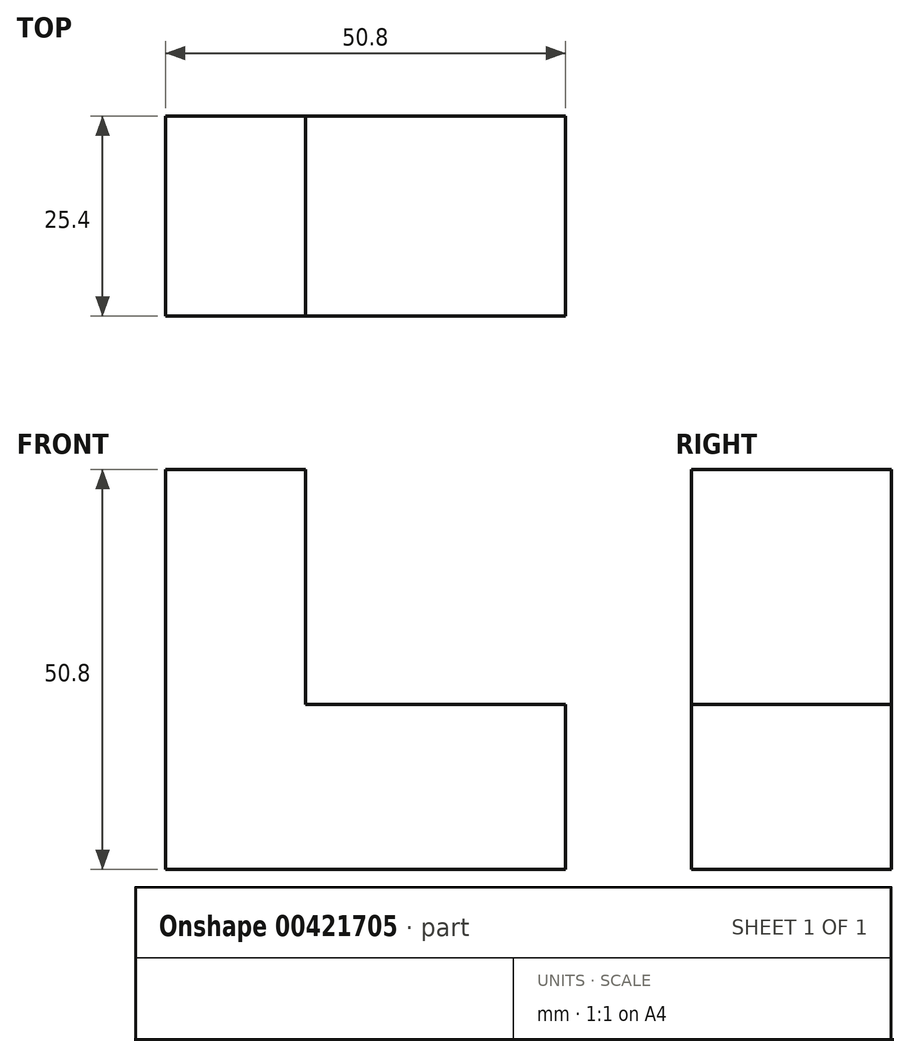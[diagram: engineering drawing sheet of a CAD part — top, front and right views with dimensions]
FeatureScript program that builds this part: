
annotation { "Feature Type Name" : "Feature", "Feature Type Description" : "" }
export const myFeature = defineFeature(function(context is Context, id is Id, definition is map)
    precondition{}
    {
        {
            var Q0;
            Q0=qCreatedBy(makeId("Front.planeOp"),FACE);
            var sketch = newSketch(context, id + "F0", { "sketchPlane" : qUnion([Q0])});
            skLineSegment(sketch, "E0", {"start": v(0, 0) * mm, "end": v(50.8, 0) * mm});
            skLineSegment(sketch, "E1", {"start": v(50.8, 0) * mm, "end": v(50.8, 50.8) * mm});
            skLineSegment(sketch, "E2", {"start": v(50.8, 50.8) * mm, "end": v(0, 50.8) * mm});
            skLineSegment(sketch, "E3", {"start": v(0, 50.8) * mm, "end": v(0, 0) * mm});
            skSolve(sketch);
        }
        {
            var Q0;
            Q0=makeQuery(id+"F0.imprint","IMPRINT",FACE,{"disambiguationData":[TD([[makeQuery(id+"F0.imprint","IMPRINT",EDGE,{"derivedFrom":sQuery(id+"F0.wireOp",EDGE,"E0")}),1.0]])]});
            extrude(context, id + "F1", {"entities" : qUnion([Q0]), "depth" : 25.4 * mm});
        }
        {
            var Q0;
            Q0=makeQuery(id+"F1.opExtrude","CAP_FACE",FACE,{"disambiguationData":[OSD([sQuery(id+"F0.wireOp",EDGE,"E0"),sQuery(id+"F0.wireOp",EDGE,"E1"),sQuery(id+"F0.wireOp",EDGE,"E2"),sQuery(id+"F0.wireOp",EDGE,"E3")])],"isStart":false});
            var sketch = newSketch(context, id + "F2", { "sketchPlane" : qUnion([Q0])});
            skLineSegment(sketch, "E4", {"start": v(17.8, 50.8) * mm, "end": v(17.8, 20.94) * mm});
            skLineSegment(sketch, "E5", {"start": v(17.8, 20.94) * mm, "end": v(50.8, 20.94) * mm});
            skLineSegment(sketch, "E6", {"start": v(50.8, 20.94) * mm, "end": v(50.8, 50.8) * mm});
            skLineSegment(sketch, "E7", {"start": v(50.8, 50.8) * mm, "end": v(17.8, 50.8) * mm});
            skSolve(sketch);
        }
        {
            var Q0;
            Q0 = qSketchRegion(id + "F2", true);
            extrude(context, id + "F3", {"entities" : qUnion([Q0]), "operationType" : NewBodyOperationType.REMOVE, "oppositeDirection" : true, "depth" : 127 * mm});
        }
    });
